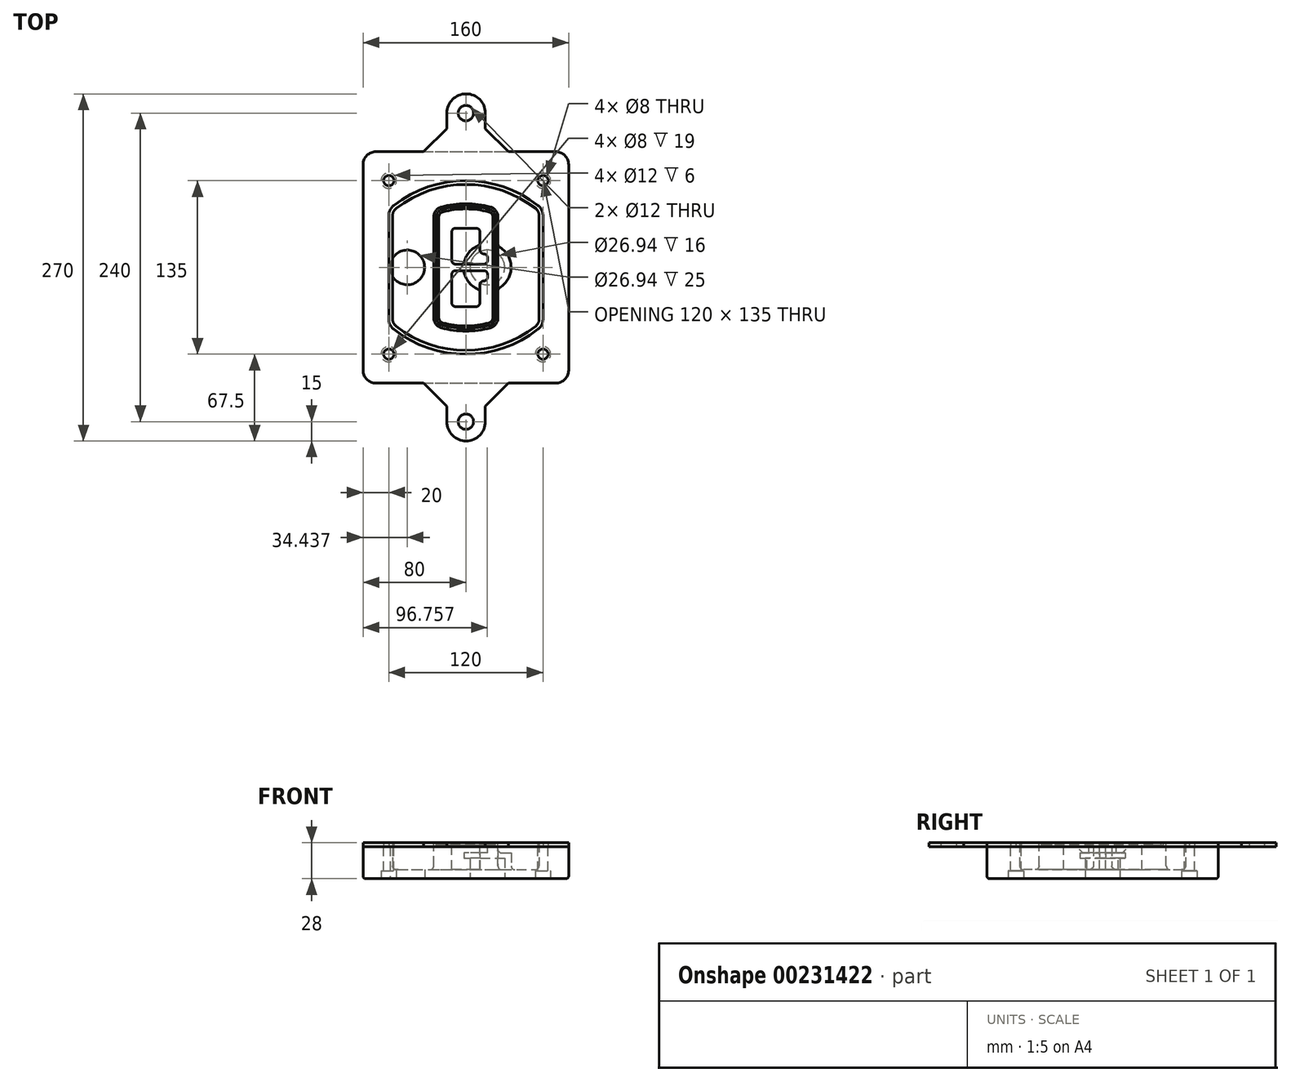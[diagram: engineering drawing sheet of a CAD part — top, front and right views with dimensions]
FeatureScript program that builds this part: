
annotation { "Feature Type Name" : "Feature", "Feature Type Description" : "" }
export const myFeature = defineFeature(function(context is Context, id is Id, definition is map)
    precondition{}
    {
        {
            var Q0;
            Q0=qCreatedBy(makeId("Top.planeOp"),FACE);
            var sketch = newSketch(context, id + "F0", { "sketchPlane" : qUnion([Q0])});
            skPoint(sketch, "E0.rect.middle", {"position": v(0, 0) * mm});
            skLineSegment(sketch, "E1.bottom", {"start": v(-70, -90) * mm, "end": v(70, -90) * mm});
            skLineSegment(sketch, "E1.top", {"start": v(-70, 90) * mm, "end": v(70, 90) * mm});
            skLineSegment(sketch, "E1.left", {"start": v(-80, -80) * mm, "end": v(-80, 80) * mm});
            skLineSegment(sketch, "E1.right", {"start": v(80, -80) * mm, "end": v(80, 80) * mm});
            skLineSegment(sketch, "E2", {"start": v(-80, 90) * mm, "end": v(80, -90) * mm, "construction": true});
            skLineSegment(sketch, "E3", {"start": v(80, 90) * mm, "end": v(-80, -90) * mm, "construction": true});
            skCircle(sketch, "E4", {"center": v(-60, 67.5) * mm, "radius": 4 * mm});
            skCircle(sketch, "E5", {"center": v(60, 67.5) * mm, "radius": 4 * mm});
            skCircle(sketch, "E6", {"center": v(60, -67.5) * mm, "radius": 4 * mm});
            skCircle(sketch, "E7", {"center": v(-60, -67.5) * mm, "radius": 4 * mm});
            skLineSegment(sketch, "E8", {"start": v(-60, 67.5) * mm, "end": v(60, 67.5) * mm, "construction": true});
            skLineSegment(sketch, "E9", {"start": v(60, 67.5) * mm, "end": v(60, -67.5) * mm, "construction": true});
            skLineSegment(sketch, "E10", {"start": v(60, -67.5) * mm, "end": v(-60, -67.5) * mm, "construction": true});
            skLineSegment(sketch, "E11", {"start": v(-60, -67.5) * mm, "end": v(-60, 67.5) * mm, "construction": true});
            skLineSegment(sketch, "E12", {"start": v(-60, 40.3) * mm, "end": v(-60, -40.3) * mm});
            skLineSegment(sketch, "E13", {"start": v(60, 40.3) * mm, "end": v(60, -40.3) * mm});
            skArc(sketch, "E14", {"start": v(56.15, 48.18) * mm, "mid": v(0, 67.5) * mm, "end": v(-56.15, 48.18) * mm});
            skArc(sketch, "E15", {"start": v(-56.15, -48.18) * mm, "mid": v(0, -67.5) * mm, "end": v(56.15, -48.18) * mm});
            skLineSegment(sketch, "E16", {"start": v(-60, 0) * mm, "end": v(60, 0) * mm, "construction": true});
            skPoint(sketch, "E17.visualSharp", {"position": v(-60, -45) * mm});
            skArc(sketch, "E17.filletArc", {"start": v(-60, -40.3) * mm, "mid": v(-58.99, -44.68) * mm, "end": v(-56.15, -48.18) * mm});
            skPoint(sketch, "E18.visualSharp", {"position": v(-60, 45) * mm});
            skArc(sketch, "E18.filletArc", {"start": v(-56.15, 48.18) * mm, "mid": v(-58.99, 44.68) * mm, "end": v(-60, 40.3) * mm});
            skPoint(sketch, "E19.visualSharp", {"position": v(60, 45) * mm});
            skArc(sketch, "E19.filletArc", {"start": v(60, 40.3) * mm, "mid": v(58.99, 44.68) * mm, "end": v(56.15, 48.18) * mm});
            skPoint(sketch, "E20.visualSharp", {"position": v(60, -45) * mm});
            skArc(sketch, "E20.filletArc", {"start": v(56.15, -48.18) * mm, "mid": v(58.99, -44.68) * mm, "end": v(60, -40.3) * mm});
            skPoint(sketch, "E21.visualSharp", {"position": v(-80, 90) * mm});
            skArc(sketch, "E21.filletArc", {"start": v(-70, 90) * mm, "mid": v(-77.07, 87.07) * mm, "end": v(-80, 80) * mm});
            skPoint(sketch, "E22.visualSharp", {"position": v(80, 90) * mm});
            skArc(sketch, "E22.filletArc", {"start": v(80, 80) * mm, "mid": v(77.07, 87.07) * mm, "end": v(70, 90) * mm});
            skPoint(sketch, "E23.visualSharp", {"position": v(80, -90) * mm});
            skArc(sketch, "E23.filletArc", {"start": v(70, -90) * mm, "mid": v(77.07, -87.07) * mm, "end": v(80, -80) * mm});
            skPoint(sketch, "E24.visualSharp", {"position": v(-80, -90) * mm});
            skArc(sketch, "E24.filletArc", {"start": v(-80, -80) * mm, "mid": v(-77.07, -87.07) * mm, "end": v(-70, -90) * mm});
            skArc(sketch, "E25.0", {"start": v(57, 40.3) * mm, "mid": v(56.3, 43.36) * mm, "end": v(54.3, 45.81) * mm});
            skLineSegment(sketch, "E25.1", {"start": v(57, 40.3) * mm, "end": v(57, -40.3) * mm});
            skArc(sketch, "E25.2", {"start": v(54.3, -45.81) * mm, "mid": v(56.3, -43.36) * mm, "end": v(57, -40.3) * mm});
            skArc(sketch, "E25.3", {"start": v(-54.3, -45.81) * mm, "mid": v(0, -64.5) * mm, "end": v(54.3, -45.81) * mm});
            skArc(sketch, "E25.4", {"start": v(-57, -40.3) * mm, "mid": v(-56.3, -43.36) * mm, "end": v(-54.3, -45.81) * mm});
            skArc(sketch, "E25.5", {"start": v(54.3, 45.81) * mm, "mid": v(0, 64.5) * mm, "end": v(-54.3, 45.81) * mm});
            skLineSegment(sketch, "E25.6", {"start": v(-57, 40.3) * mm, "end": v(-57, -40.3) * mm});
            skArc(sketch, "E25.7", {"start": v(-54.3, 45.81) * mm, "mid": v(-56.3, 43.36) * mm, "end": v(-57, 40.3) * mm});
            skArc(sketch, "E26.0", {"start": v(-58.62, 51.33) * mm, "mid": v(-62.58, 46.43) * mm, "end": v(-64, 40.3) * mm});
            skArc(sketch, "E26.1", {"start": v(58.62, 51.33) * mm, "mid": v(0, 71.5) * mm, "end": v(-58.62, 51.33) * mm});
            skArc(sketch, "E26.2", {"start": v(64, 40.3) * mm, "mid": v(62.58, 46.43) * mm, "end": v(58.62, 51.33) * mm});
            skLineSegment(sketch, "E26.3", {"start": v(64, 40.3) * mm, "end": v(64, -40.3) * mm});
            skArc(sketch, "E26.4", {"start": v(58.62, -51.33) * mm, "mid": v(62.58, -46.43) * mm, "end": v(64, -40.3) * mm});
            skLineSegment(sketch, "E26.5", {"start": v(-64, 40.3) * mm, "end": v(-64, -40.3) * mm});
            skArc(sketch, "E26.6", {"start": v(-58.62, -51.33) * mm, "mid": v(0, -71.5) * mm, "end": v(58.62, -51.33) * mm});
            skArc(sketch, "E26.7", {"start": v(-64, -40.3) * mm, "mid": v(-62.58, -46.43) * mm, "end": v(-58.62, -51.33) * mm});
            skSolve(sketch);
        }
        {
            var Q0;
            Q0=makeQuery(id+"F0.imprint","IMPRINT",FACE,{"disambiguationData":[TD([[makeQuery(id+"F0.imprint","IMPRINT",EDGE,{"derivedFrom":sQuery(id+"F0.wireOp",EDGE,"E1.bottom")}),1.0]])]});
            var Q1;
            Q1=makeQuery(id+"F0.imprint","IMPRINT",FACE,{"disambiguationData":[TD([[makeQuery(id+"F0.imprint","IMPRINT",EDGE,{"derivedFrom":sQuery(id+"F0.wireOp",EDGE,"E12")}),1.0]])]});
            var Q2;
            Q2=makeQuery(id+"F0.imprint","IMPRINT",FACE,{"disambiguationData":[TD([[makeQuery(id+"F0.imprint","IMPRINT",EDGE,{"derivedFrom":sQuery(id+"F0.wireOp",EDGE,"E25.0")}),1.0]])]});
            var Q3;
            Q3=makeQuery(id+"F0.imprint","IMPRINT",FACE,{"disambiguationData":[TD([[makeQuery(id+"F0.imprint","IMPRINT",EDGE,{"derivedFrom":sQuery(id+"F0.wireOp",EDGE,"E12")}),-1.0]])]});
            extrude(context, id + "F1", {"entities" : qUnion([Q0, Q1, Q2, Q3]), "oppositeDirection" : true, "depth" : 25 * mm});
        }
        {
            var Q0;
            Q0=makeQuery(id+"F0.imprint","IMPRINT",FACE,{"disambiguationData":[TD([[makeQuery(id+"F0.imprint","IMPRINT",EDGE,{"derivedFrom":sQuery(id+"F0.wireOp",EDGE,"E12")}),1.0]])]});
            extrude(context, id + "F2", {"entities" : qUnion([Q0]), "operationType" : NewBodyOperationType.ADD, "depth" : 3 * mm});
        }
        {
            var Q0;
            Q0=makeQuery(id+"F0.imprint","IMPRINT",FACE,{"disambiguationData":[TD([[makeQuery(id+"F0.imprint","IMPRINT",EDGE,{"derivedFrom":sQuery(id+"F0.wireOp",EDGE,"E25.0")}),1.0]])]});
            extrude(context, id + "F3", {"entities" : qUnion([Q0]), "operationType" : NewBodyOperationType.REMOVE, "oppositeDirection" : true, "depth" : 18 * mm});
        }
        {
            var Q0;
            Q0=makeQuery(id+"F2.opExtrude","CAP_FACE",FACE,{"disambiguationData":[OSD([sQuery(id+"F0.wireOp",EDGE,"E12"),sQuery(id+"F0.wireOp",EDGE,"E13"),sQuery(id+"F0.wireOp",EDGE,"E14"),sQuery(id+"F0.wireOp",EDGE,"E15"),sQuery(id+"F0.wireOp",EDGE,"E17.filletArc"),sQuery(id+"F0.wireOp",EDGE,"E18.filletArc"),sQuery(id+"F0.wireOp",EDGE,"E19.filletArc"),sQuery(id+"F0.wireOp",EDGE,"E20.filletArc"),sQuery(id+"F0.wireOp",EDGE,"E25.0"),sQuery(id+"F0.wireOp",EDGE,"E25.1"),sQuery(id+"F0.wireOp",EDGE,"E25.2"),sQuery(id+"F0.wireOp",EDGE,"E25.3"),sQuery(id+"F0.wireOp",EDGE,"E25.4"),sQuery(id+"F0.wireOp",EDGE,"E25.5"),sQuery(id+"F0.wireOp",EDGE,"E25.6"),sQuery(id+"F0.wireOp",EDGE,"E25.7")])],"isStart":false});
            var sketch = newSketch(context, id + "F4", { "sketchPlane" : qUnion([Q0])});
            skArc(sketch, "E27.0", {"start": v(-19.08, -46.97) * mm, "mid": v(0, -49.5) * mm, "end": v(19.08, -46.97) * mm});
            skArc(sketch, "E28.0", {"start": v(19.08, 46.97) * mm, "mid": v(0, 49.5) * mm, "end": v(-19.08, 46.97) * mm});
            skLineSegment(sketch, "E29", {"start": v(-25, 39.25) * mm, "end": v(-25, -39.25) * mm});
            skLineSegment(sketch, "E30", {"start": v(25, 39.25) * mm, "end": v(25, -39.25) * mm});
            skLineSegment(sketch, "E31", {"start": v(-25, 45.1) * mm, "end": v(25, 45.1) * mm, "construction": true});
            skLineSegment(sketch, "E32", {"start": v(-25, -45.1) * mm, "end": v(25, -45.1) * mm, "construction": true});
            skPoint(sketch, "E33.visualSharp", {"position": v(-25, 45.1) * mm});
            skArc(sketch, "E33.filletArc", {"start": v(-19.08, 46.97) * mm, "mid": v(-23.35, 44.11) * mm, "end": v(-25, 39.25) * mm});
            skPoint(sketch, "E34.visualSharp", {"position": v(25, 45.1) * mm});
            skArc(sketch, "E34.filletArc", {"start": v(25, 39.25) * mm, "mid": v(23.35, 44.11) * mm, "end": v(19.08, 46.97) * mm});
            skPoint(sketch, "E35.visualSharp", {"position": v(25, -45.1) * mm});
            skArc(sketch, "E35.filletArc", {"start": v(19.08, -46.97) * mm, "mid": v(23.35, -44.11) * mm, "end": v(25, -39.25) * mm});
            skPoint(sketch, "E36.visualSharp", {"position": v(-25, -45.1) * mm});
            skArc(sketch, "E36.filletArc", {"start": v(-25, -39.25) * mm, "mid": v(-23.35, -44.11) * mm, "end": v(-19.08, -46.97) * mm});
            skArc(sketch, "E37.0", {"start": v(54.3, 45.81) * mm, "mid": v(0, 64.5) * mm, "end": v(-54.3, 45.81) * mm});
            skArc(sketch, "E37.1", {"start": v(-54.3, 45.81) * mm, "mid": v(-56.3, 43.36) * mm, "end": v(-57, 40.3) * mm});
            skLineSegment(sketch, "E37.2", {"start": v(-57, 40.3) * mm, "end": v(-57, -40.3) * mm});
            skArc(sketch, "E37.3", {"start": v(-57, -40.3) * mm, "mid": v(-56.3, -43.36) * mm, "end": v(-54.3, -45.81) * mm});
            skArc(sketch, "E37.4", {"start": v(-54.3, -45.81) * mm, "mid": v(0, -64.5) * mm, "end": v(54.3, -45.81) * mm});
            skArc(sketch, "E37.5", {"start": v(54.3, -45.81) * mm, "mid": v(56.3, -43.36) * mm, "end": v(57, -40.3) * mm});
            skLineSegment(sketch, "E37.6", {"start": v(57, 40.3) * mm, "end": v(57, -40.3) * mm});
            skArc(sketch, "E37.7", {"start": v(57, 40.3) * mm, "mid": v(56.3, 43.36) * mm, "end": v(54.3, 45.81) * mm});
            skLineSegment(sketch, "E38.0", {"start": v(23, 39.25) * mm, "end": v(23, -39.25) * mm});
            skArc(sketch, "E38.1", {"start": v(18.56, -45.04) * mm, "mid": v(21.76, -42.9) * mm, "end": v(23, -39.25) * mm});
            skArc(sketch, "E38.2", {"start": v(-18.56, -45.04) * mm, "mid": v(0, -47.5) * mm, "end": v(18.56, -45.04) * mm});
            skArc(sketch, "E38.3", {"start": v(-23, -39.25) * mm, "mid": v(-21.76, -42.9) * mm, "end": v(-18.56, -45.04) * mm});
            skLineSegment(sketch, "E38.4", {"start": v(-23, 39.25) * mm, "end": v(-23, -39.25) * mm});
            skArc(sketch, "E38.5", {"start": v(23, 39.25) * mm, "mid": v(21.76, 42.9) * mm, "end": v(18.56, 45.04) * mm});
            skArc(sketch, "E38.6", {"start": v(-18.56, 45.04) * mm, "mid": v(-21.76, 42.9) * mm, "end": v(-23, 39.25) * mm});
            skArc(sketch, "E38.7", {"start": v(18.56, 45.04) * mm, "mid": v(0, 47.5) * mm, "end": v(-18.56, 45.04) * mm});
            skArc(sketch, "E39.0", {"start": v(21, 39.25) * mm, "mid": v(20.18, 41.68) * mm, "end": v(18.04, 43.1) * mm});
            skLineSegment(sketch, "E39.1", {"start": v(21, 39.25) * mm, "end": v(21, -39.25) * mm});
            skArc(sketch, "E39.2", {"start": v(18.04, -43.1) * mm, "mid": v(20.18, -41.68) * mm, "end": v(21, -39.25) * mm});
            skArc(sketch, "E39.3", {"start": v(-18.04, -43.1) * mm, "mid": v(0, -45.5) * mm, "end": v(18.04, -43.1) * mm});
            skArc(sketch, "E39.4", {"start": v(-21, -39.25) * mm, "mid": v(-20.18, -41.68) * mm, "end": v(-18.04, -43.1) * mm});
            skArc(sketch, "E39.5", {"start": v(18.04, 43.1) * mm, "mid": v(0, 45.5) * mm, "end": v(-18.04, 43.1) * mm});
            skLineSegment(sketch, "E39.6", {"start": v(-21, 39.25) * mm, "end": v(-21, -39.25) * mm});
            skArc(sketch, "E39.7", {"start": v(-18.04, 43.1) * mm, "mid": v(-20.18, 41.68) * mm, "end": v(-21, 39.25) * mm});
            skLineSegment(sketch, "E40", {"start": v(-25, 0) * mm, "end": v(25, 0) * mm, "construction": true});
            skLineSegment(sketch, "E41", {"start": v(-11, 5.5) * mm, "end": v(-11, 27.5) * mm});
            skLineSegment(sketch, "E42", {"start": v(-8, 30.5) * mm, "end": v(8, 30.5) * mm});
            skLineSegment(sketch, "E43", {"start": v(11, 27.5) * mm, "end": v(11, 13.5) * mm});
            skLineSegment(sketch, "E44", {"start": v(14, 10.5) * mm, "end": v(14, 10.5) * mm});
            skLineSegment(sketch, "E45", {"start": v(17, 7.5) * mm, "end": v(17, 5.5) * mm});
            skLineSegment(sketch, "E46", {"start": v(14, 2.5) * mm, "end": v(-8, 2.5) * mm});
            skPoint(sketch, "E47.visualSharp", {"position": v(-11, 30.5) * mm});
            skArc(sketch, "E47.filletArc", {"start": v(-8, 30.5) * mm, "mid": v(-10.12, 29.62) * mm, "end": v(-11, 27.5) * mm});
            skPoint(sketch, "E48.visualSharp", {"position": v(11, 30.5) * mm});
            skArc(sketch, "E48.filletArc", {"start": v(11, 27.5) * mm, "mid": v(10.12, 29.62) * mm, "end": v(8, 30.5) * mm});
            skPoint(sketch, "E49.visualSharp", {"position": v(11, 10.5) * mm});
            skArc(sketch, "E49.filletArc", {"start": v(11, 13.5) * mm, "mid": v(11.88, 11.38) * mm, "end": v(14, 10.5) * mm});
            skPoint(sketch, "E50.visualSharp", {"position": v(17, 10.5) * mm});
            skArc(sketch, "E50.filletArc", {"start": v(17, 7.5) * mm, "mid": v(16.12, 9.62) * mm, "end": v(14, 10.5) * mm});
            skPoint(sketch, "E51.visualSharp", {"position": v(17, 2.5) * mm});
            skArc(sketch, "E51.filletArc", {"start": v(14, 2.5) * mm, "mid": v(16.12, 3.38) * mm, "end": v(17, 5.5) * mm});
            skPoint(sketch, "E52.visualSharp", {"position": v(-11, 2.5) * mm});
            skArc(sketch, "E52.filletArc", {"start": v(-11, 5.5) * mm, "mid": v(-10.12, 3.38) * mm, "end": v(-8, 2.5) * mm});
            skLineSegment(sketch, "E53.0.MirrorCS", {"start": v(14, -2.5) * mm, "end": v(-8, -2.5) * mm});
            skArc(sketch, "E54.0.MirrorCS", {"start": v(-11, -5.5) * mm, "mid": v(-10.12, -3.38) * mm, "end": v(-8, -2.5) * mm});
            skLineSegment(sketch, "E55.0.MirrorCS", {"start": v(-11, -5.5) * mm, "end": v(-11, -27.5) * mm});
            skArc(sketch, "E56.0.MirrorCS", {"start": v(-8, -30.5) * mm, "mid": v(-10.12, -29.62) * mm, "end": v(-11, -27.5) * mm});
            skLineSegment(sketch, "E57.0.MirrorCS", {"start": v(-8, -30.5) * mm, "end": v(8, -30.5) * mm});
            skArc(sketch, "E58.0.MirrorCS", {"start": v(11, -27.5) * mm, "mid": v(10.12, -29.62) * mm, "end": v(8, -30.5) * mm});
            skLineSegment(sketch, "E59.0.MirrorCS", {"start": v(11, -27.5) * mm, "end": v(11, -13.5) * mm});
            skArc(sketch, "E60.0.MirrorCS", {"start": v(11, -13.5) * mm, "mid": v(11.88, -11.38) * mm, "end": v(14, -10.5) * mm});
            skArc(sketch, "E61.0.MirrorCS", {"start": v(17, -7.5) * mm, "mid": v(16.12, -9.62) * mm, "end": v(14, -10.5) * mm});
            skLineSegment(sketch, "E62.0.MirrorCS", {"start": v(17, -7.5) * mm, "end": v(17, -5.5) * mm});
            skArc(sketch, "E63.0.MirrorCS", {"start": v(14, -2.5) * mm, "mid": v(16.12, -3.38) * mm, "end": v(17, -5.5) * mm});
            skSolve(sketch);
        }
        {
            var Q0;
            Q0=makeQuery(id+"F4.imprint","IMPRINT",FACE,{"disambiguationData":[TD([[makeQuery(id+"F4.imprint","IMPRINT",EDGE,{"derivedFrom":sQuery(id+"F4.wireOp",EDGE,"E27.0")}),1.0]])]});
            var Q1;
            Q1=makeQuery(id+"F4.imprint","IMPRINT",FACE,{"disambiguationData":[TD([[makeQuery(id+"F4.imprint","IMPRINT",EDGE,{"derivedFrom":sQuery(id+"F4.wireOp",EDGE,"E38.0")}),-1.0]])]});
            var Q2;
            Q2=makeQuery(id+"F4.imprint","IMPRINT",FACE,{"disambiguationData":[TD([[makeQuery(id+"F4.imprint","IMPRINT",EDGE,{"derivedFrom":sQuery(id+"F4.wireOp",EDGE,"E39.0")}),1.0]])]});
            extrude(context, id + "F5", {"entities" : qUnion([Q0, Q1, Q2]), "operationType" : NewBodyOperationType.ADD, "endBound" : BoundingType.UP_TO_NEXT, "oppositeDirection" : true, "depth" : 25 * mm});
        }
        {
            var Q0;
            Q0=makeQuery(id+"F4.imprint","IMPRINT",FACE,{"disambiguationData":[TD([[makeQuery(id+"F4.imprint","IMPRINT",EDGE,{"derivedFrom":sQuery(id+"F4.wireOp",EDGE,"E38.0")}),-1.0]])]});
            extrude(context, id + "F6", {"entities" : qUnion([Q0]), "operationType" : NewBodyOperationType.REMOVE, "oppositeDirection" : true, "depth" : 2 * mm});
        }
        {
            var Q0;
            Q0=makeQuery(id+"F1.opExtrude","CAP_FACE",FACE,{"disambiguationData":[OSD([sQuery(id+"F0.wireOp",EDGE,"E1.bottom"),sQuery(id+"F0.wireOp",EDGE,"E1.top"),sQuery(id+"F0.wireOp",EDGE,"E1.left"),sQuery(id+"F0.wireOp",EDGE,"E1.right"),sQuery(id+"F0.wireOp",EDGE,"E4"),sQuery(id+"F0.wireOp",EDGE,"E5"),sQuery(id+"F0.wireOp",EDGE,"E6"),sQuery(id+"F0.wireOp",EDGE,"E7"),sQuery(id+"F0.wireOp",EDGE,"E21.filletArc"),sQuery(id+"F0.wireOp",EDGE,"E22.filletArc"),sQuery(id+"F0.wireOp",EDGE,"E23.filletArc"),sQuery(id+"F0.wireOp",EDGE,"E24.filletArc")])],"isStart":false});
            var sketch = newSketch(context, id + "F7", { "sketchPlane" : qUnion([Q0])});
            skCircle(sketch, "E64", {"center": v(16.76, 0) * mm, "radius": 13.47 * mm});
            skCircle(sketch, "E65", {"center": v(-45.56, 0) * mm, "radius": 13.47 * mm});
            skLineSegment(sketch, "E66", {"start": v(80, 0) * mm, "end": v(-80, 0) * mm});
            skCircle(sketch, "E67", {"center": v(16.76, 0) * mm, "radius": 18.47 * mm});
            skCircle(sketch, "E68", {"center": v(60, -67.5) * mm, "radius": 6 * mm});
            skCircle(sketch, "E69", {"center": v(-60, -67.5) * mm, "radius": 6 * mm});
            skCircle(sketch, "E70", {"center": v(-60, 67.5) * mm, "radius": 6 * mm});
            skCircle(sketch, "E71", {"center": v(60, 67.5) * mm, "radius": 6 * mm});
            skSolve(sketch);
        }
        {
            var Q0;
            {var subQ1=sQuery(id+"F7.wireOp",EDGE,"E66");var subQ4=sQuery(id+"F7.wireOp",EDGE,"E64");var subQ6=makeQuery(id+"F7.imprint","INTERSECT",VERTEX,{"disambiguationData":[OD(0.0)],"derivedFrom":[subQ4,subQ1]});Q0=makeQuery(id+"F7.imprint","IMPRINT",FACE,{"disambiguationData":[TD([[makeQuery(id+"F7.imprint","IMPRINT",EDGE,{"disambiguationData":[TD([[subQ6,-1.0]])],"derivedFrom":subQ4}),-1.0]])]});}
            var Q1;
            {var subQ0=sQuery(id+"F7.wireOp",EDGE,"E66");var subQ1=sQuery(id+"F7.wireOp",EDGE,"E64");var subQ3=makeQuery(id+"F7.imprint","INTERSECT",VERTEX,{"disambiguationData":[OD(0.0)],"derivedFrom":[subQ1,subQ0]});Q1=makeQuery(id+"F7.imprint","IMPRINT",FACE,{"disambiguationData":[TD([[makeQuery(id+"F7.imprint","IMPRINT",EDGE,{"disambiguationData":[TD([[subQ3,-1.0]])],"derivedFrom":subQ1}),1.0]])]});}
            var Q2;
            {var subQ0=sQuery(id+"F7.wireOp",EDGE,"E66");var subQ1=sQuery(id+"F7.wireOp",EDGE,"E64");var subQ3=makeQuery(id+"F7.imprint","INTERSECT",VERTEX,{"disambiguationData":[OD(0.0)],"derivedFrom":[subQ1,subQ0]});Q2=makeQuery(id+"F7.imprint","IMPRINT",FACE,{"disambiguationData":[TD([[makeQuery(id+"F7.imprint","IMPRINT",EDGE,{"disambiguationData":[TD([[subQ3,1.0]])],"derivedFrom":subQ1}),1.0]])]});}
            var Q3;
            {var subQ1=sQuery(id+"F7.wireOp",EDGE,"E66");var subQ4=sQuery(id+"F7.wireOp",EDGE,"E64");var subQ6=makeQuery(id+"F7.imprint","INTERSECT",VERTEX,{"disambiguationData":[OD(0.0)],"derivedFrom":[subQ4,subQ1]});Q3=makeQuery(id+"F7.imprint","IMPRINT",FACE,{"disambiguationData":[TD([[makeQuery(id+"F7.imprint","IMPRINT",EDGE,{"disambiguationData":[TD([[subQ6,1.0]])],"derivedFrom":subQ4}),-1.0]])]});}
            extrude(context, id + "F8", {"entities" : qUnion([Q0, Q1, Q2, Q3]), "operationType" : NewBodyOperationType.ADD, "oppositeDirection" : true, "depth" : 20 * mm});
        }
        {
            var Q0;
            {var subQ0=sQuery(id+"F7.wireOp",EDGE,"E66");var subQ1=sQuery(id+"F7.wireOp",EDGE,"E64");var subQ3=makeQuery(id+"F7.imprint","INTERSECT",VERTEX,{"disambiguationData":[OD(0.0)],"derivedFrom":[subQ1,subQ0]});Q0=makeQuery(id+"F7.imprint","IMPRINT",FACE,{"disambiguationData":[TD([[makeQuery(id+"F7.imprint","IMPRINT",EDGE,{"disambiguationData":[TD([[subQ3,-1.0]])],"derivedFrom":subQ1}),1.0]])]});}
            var Q1;
            {var subQ0=sQuery(id+"F7.wireOp",EDGE,"E66");var subQ1=sQuery(id+"F7.wireOp",EDGE,"E64");var subQ3=makeQuery(id+"F7.imprint","INTERSECT",VERTEX,{"disambiguationData":[OD(0.0)],"derivedFrom":[subQ1,subQ0]});Q1=makeQuery(id+"F7.imprint","IMPRINT",FACE,{"disambiguationData":[TD([[makeQuery(id+"F7.imprint","IMPRINT",EDGE,{"disambiguationData":[TD([[subQ3,1.0]])],"derivedFrom":subQ1}),1.0]])]});}
            extrude(context, id + "F9", {"entities" : qUnion([Q0, Q1]), "operationType" : NewBodyOperationType.REMOVE, "oppositeDirection" : true, "depth" : 16 * mm});
        }
        {
            var Q0;
            {var subQ0=sQuery(id+"F7.wireOp",EDGE,"E66");var subQ1=sQuery(id+"F7.wireOp",EDGE,"E65");var subQ3=makeQuery(id+"F7.imprint","INTERSECT",VERTEX,{"disambiguationData":[OD(0.0)],"derivedFrom":[subQ1,subQ0]});Q0=makeQuery(id+"F7.imprint","IMPRINT",FACE,{"disambiguationData":[TD([[makeQuery(id+"F7.imprint","IMPRINT",EDGE,{"disambiguationData":[TD([[subQ3,-1.0]])],"derivedFrom":subQ1}),1.0]])]});}
            var Q1;
            {var subQ0=sQuery(id+"F7.wireOp",EDGE,"E66");var subQ1=sQuery(id+"F7.wireOp",EDGE,"E65");var subQ3=makeQuery(id+"F7.imprint","INTERSECT",VERTEX,{"disambiguationData":[OD(0.0)],"derivedFrom":[subQ1,subQ0]});Q1=makeQuery(id+"F7.imprint","IMPRINT",FACE,{"disambiguationData":[TD([[makeQuery(id+"F7.imprint","IMPRINT",EDGE,{"disambiguationData":[TD([[subQ3,1.0]])],"derivedFrom":subQ1}),1.0]])]});}
            extrude(context, id + "F10", {"entities" : qUnion([Q0, Q1]), "operationType" : NewBodyOperationType.REMOVE, "oppositeDirection" : true, "depth" : 25 * mm});
        }
        {
            var Q0;
            Q0=makeQuery(id+"F7.imprint","IMPRINT",FACE,{"disambiguationData":[TD([[makeQuery(id+"F7.imprint","IMPRINT",EDGE,{"derivedFrom":sQuery(id+"F7.wireOp",EDGE,"E68")}),1.0]])]});
            var Q1;
            Q1=makeQuery(id+"F7.imprint","IMPRINT",FACE,{"disambiguationData":[TD([[makeQuery(id+"F7.imprint","IMPRINT",EDGE,{"derivedFrom":makeQuery(id+"F1.opExtrude","CAP_EDGE",EDGE,{"disambiguationData":[OSD([sQuery(id+"F0.wireOp",EDGE,"E5")])],"isStart":false})}),-1.0]])]});
            var Q2;
            Q2=makeQuery(id+"F7.imprint","IMPRINT",FACE,{"disambiguationData":[TD([[makeQuery(id+"F7.imprint","IMPRINT",EDGE,{"derivedFrom":sQuery(id+"F7.wireOp",EDGE,"E69")}),1.0]])]});
            var Q3;
            Q3=makeQuery(id+"F7.imprint","IMPRINT",FACE,{"disambiguationData":[TD([[makeQuery(id+"F7.imprint","IMPRINT",EDGE,{"derivedFrom":makeQuery(id+"F1.opExtrude","CAP_EDGE",EDGE,{"disambiguationData":[OSD([sQuery(id+"F0.wireOp",EDGE,"E4")])],"isStart":false})}),-1.0]])]});
            var Q4;
            Q4=makeQuery(id+"F7.imprint","IMPRINT",FACE,{"disambiguationData":[TD([[makeQuery(id+"F7.imprint","IMPRINT",EDGE,{"derivedFrom":sQuery(id+"F7.wireOp",EDGE,"E70")}),1.0]])]});
            var Q5;
            Q5=makeQuery(id+"F7.imprint","IMPRINT",FACE,{"disambiguationData":[TD([[makeQuery(id+"F7.imprint","IMPRINT",EDGE,{"derivedFrom":makeQuery(id+"F1.opExtrude","CAP_EDGE",EDGE,{"disambiguationData":[OSD([sQuery(id+"F0.wireOp",EDGE,"E7")])],"isStart":false})}),-1.0]])]});
            var Q6;
            Q6=makeQuery(id+"F7.imprint","IMPRINT",FACE,{"disambiguationData":[TD([[makeQuery(id+"F7.imprint","IMPRINT",EDGE,{"derivedFrom":sQuery(id+"F7.wireOp",EDGE,"E71")}),1.0]])]});
            var Q7;
            Q7=makeQuery(id+"F7.imprint","IMPRINT",FACE,{"disambiguationData":[TD([[makeQuery(id+"F7.imprint","IMPRINT",EDGE,{"derivedFrom":makeQuery(id+"F1.opExtrude","CAP_EDGE",EDGE,{"disambiguationData":[OSD([sQuery(id+"F0.wireOp",EDGE,"E6")])],"isStart":false})}),-1.0]])]});
            extrude(context, id + "F11", {"entities" : qUnion([Q0, Q1, Q2, Q3, Q4, Q5, Q6, Q7]), "operationType" : NewBodyOperationType.REMOVE, "oppositeDirection" : true, "depth" : 6 * mm});
        }
        {
            var Q0;
            Q0=makeQuery(id+"F9.boolean.opBoolean","COPY",FACE,{"derivedFrom":makeQuery(id+"F9.opExtrude","CAP_FACE",FACE,{"disambiguationData":[OSD([sQuery(id+"F7.wireOp",EDGE,"E64")])],"isStart":false})});
            var sketch = newSketch(context, id + "F12", { "sketchPlane" : qUnion([Q0])});
            skArc(sketch, "E72.0", {"start": v(11, 17.55) * mm, "mid": v(2.57, 11.82) * mm, "end": v(-1.54, 2.5) * mm});
            skArc(sketch, "E72.1", {"start": v(-1.54, -2.5) * mm, "mid": v(2.57, -11.82) * mm, "end": v(11, -17.55) * mm});
            skLineSegment(sketch, "E73", {"start": v(-1.54, -2.5) * mm, "end": v(14, -2.5) * mm});
            skLineSegment(sketch, "E74.0", {"start": v(14, 2.5) * mm, "end": v(-1.54, 2.5) * mm});
            skArc(sketch, "E74.1", {"start": v(14, 2.5) * mm, "mid": v(16.12, 3.38) * mm, "end": v(17, 5.5) * mm});
            skLineSegment(sketch, "E74.2", {"start": v(17, 7.5) * mm, "end": v(17, 5.5) * mm});
            skArc(sketch, "E74.3", {"start": v(17, 7.5) * mm, "mid": v(16.12, 9.62) * mm, "end": v(14, 10.5) * mm});
            skArc(sketch, "E74.4", {"start": v(11, 13.5) * mm, "mid": v(11.88, 11.38) * mm, "end": v(14, 10.5) * mm});
            skLineSegment(sketch, "E74.5", {"start": v(11, 17.55) * mm, "end": v(11, 13.5) * mm});
            skLineSegment(sketch, "E74.7", {"start": v(14, -2.5) * mm, "end": v(-1.54, -2.5) * mm});
            skArc(sketch, "E74.8", {"start": v(14, -2.5) * mm, "mid": v(16.12, -3.38) * mm, "end": v(17, -5.5) * mm});
            skLineSegment(sketch, "E74.9", {"start": v(17, -7.5) * mm, "end": v(17, -5.5) * mm});
            skArc(sketch, "E74.10", {"start": v(17, -7.5) * mm, "mid": v(16.12, -9.62) * mm, "end": v(14, -10.5) * mm});
            skArc(sketch, "E74.11", {"start": v(11, -13.5) * mm, "mid": v(11.88, -11.38) * mm, "end": v(14, -10.5) * mm});
            skLineSegment(sketch, "E74.12", {"start": v(11, -17.55) * mm, "end": v(11, -13.5) * mm});
            skPoint(sketch, "E75.orphan", {"position": v(11, -27.5) * mm});
            skPoint(sketch, "E76.orphan", {"position": v(-8, -2.5) * mm});
            skPoint(sketch, "E77.orphan", {"position": v(-8, 2.5) * mm});
            skPoint(sketch, "E78.orphan", {"position": v(11, 27.5) * mm});
            skSolve(sketch);
        }
        {
            var Q0;
            {var subQ7=sQuery(id+"F12.wireOp",EDGE,"E72.0");var subQ14=sQuery(id+"F12.wireOp",EDGE,"E72.1");var subQ16=sQuery(id+"F12.wireOp",EDGE,"E74.1");var subQ18=sQuery(id+"F12.wireOp",EDGE,"E74.8");Q0=qUnion([makeQuery(id+"F12.imprint","IMPRINT",FACE,{"disambiguationData":[TD([[makeQuery(id+"F12.imprint","IMPRINT",EDGE,{"derivedFrom":subQ7}),1.0]])]}),makeQuery(id+"F12.imprint","IMPRINT",FACE,{"disambiguationData":[TD([[makeQuery(id+"F12.imprint","IMPRINT",EDGE,{"derivedFrom":subQ14}),1.0]])]}),makeQuery(id+"F12.imprint","IMPRINT",FACE,{"disambiguationData":[TD([[makeQuery(id+"F12.imprint","IMPRINT",EDGE,{"derivedFrom":subQ16}),1.0]])]}),makeQuery(id+"F12.imprint","IMPRINT",FACE,{"disambiguationData":[TD([[makeQuery(id+"F12.imprint","IMPRINT",EDGE,{"derivedFrom":subQ18}),-1.0]])]})]);}
            var Q1;
            Q1=makeQuery(id+"F5.boolean.opBoolean","SPLIT",FACE,{"disambiguationData":[TD([makeQuery(id+"F5.opExtrude","SWEPT_FACE",FACE,{"disambiguationData":[OSD([sQuery(id+"F4.wireOp",EDGE,"E41")])]})])],"derivedFrom":makeQuery(id+"F3.boolean.opBoolean","COPY",FACE,{"derivedFrom":makeQuery(id+"F3.opExtrude","CAP_FACE",FACE,{"disambiguationData":[OSD([sQuery(id+"F0.wireOp",EDGE,"E25.0"),sQuery(id+"F0.wireOp",EDGE,"E25.1"),sQuery(id+"F0.wireOp",EDGE,"E25.2"),sQuery(id+"F0.wireOp",EDGE,"E25.3"),sQuery(id+"F0.wireOp",EDGE,"E25.4"),sQuery(id+"F0.wireOp",EDGE,"E25.5"),sQuery(id+"F0.wireOp",EDGE,"E25.6"),sQuery(id+"F0.wireOp",EDGE,"E25.7")])],"isStart":false})})});
            extrude(context, id + "F13", {"entities" : qUnion([Q0]), "operationType" : NewBodyOperationType.REMOVE, "endBound" : BoundingType.UP_TO_SURFACE, "endBoundEntityFace" : qUnion([Q1]), "depth" : 25 * mm});
        }
        {
            var Q0;
            Q0=makeQuery(id+"F3.boolean.opBoolean","COPY",EDGE,{"derivedFrom":makeQuery(id+"F3.opExtrude","CAP_EDGE",EDGE,{"disambiguationData":[OSD([sQuery(id+"F0.wireOp",EDGE,"E25.6")])],"isStart":false})});
            var Q1;
            Q1=makeQuery(id+"F8.boolean.opBoolean","INTERSECT",EDGE,{"derivedFrom":[makeQuery(id+"F5.opExtrude","SWEPT_FACE",FACE,{"disambiguationData":[OSD([sQuery(id+"F4.wireOp",EDGE,"E30")])]}),makeQuery(id+"F8.opExtrude","CAP_FACE",FACE,{"disambiguationData":[OSD([sQuery(id+"F7.wireOp",EDGE,"E67")])],"isStart":false})]});
            var Q2;
            Q2=makeQuery(id+"F8.boolean.opBoolean","INTERSECT",EDGE,{"disambiguationData":[OD(1.0)],"derivedFrom":[makeQuery(id+"F5.opExtrude","SWEPT_FACE",FACE,{"disambiguationData":[OSD([sQuery(id+"F4.wireOp",EDGE,"E30")])]}),makeQuery(id+"F8.opExtrude","SWEPT_FACE",FACE,{"disambiguationData":[OSD([sQuery(id+"F7.wireOp",EDGE,"E67")])]})]});
            var Q3;
            {var subQ0=sQuery(id+"F4.wireOp",EDGE,"E30");Q3=makeQuery(id+"F8.boolean.opBoolean","SPLIT",EDGE,{"disambiguationData":[TD([makeQuery(id+"F5.opExtrude","SWEPT_FACE",FACE,{"disambiguationData":[OSD([sQuery(id+"F4.wireOp",EDGE,"E35.filletArc")])]})])],"derivedFrom":makeQuery(id+"F5.opExtrude","CAP_EDGE",EDGE,{"disambiguationData":[OSD([subQ0])],"isStart":false})});}
            var Q4;
            {var subQ0=sQuery(id+"F0.wireOp",EDGE,"E25.7");var subQ1=sQuery(id+"F0.wireOp",EDGE,"E25.1");var subQ2=sQuery(id+"F0.wireOp",EDGE,"E25.6");var subQ3=sQuery(id+"F0.wireOp",EDGE,"E25.5");var subQ4=sQuery(id+"F0.wireOp",EDGE,"E25.4");var subQ5=sQuery(id+"F0.wireOp",EDGE,"E25.0");var subQ6=sQuery(id+"F0.wireOp",EDGE,"E25.2");var subQ7=sQuery(id+"F0.wireOp",EDGE,"E25.3");Q4=makeQuery(id+"F8.boolean.opBoolean","INTERSECT",EDGE,{"derivedFrom":[makeQuery(id+"F5.boolean.opBoolean","SPLIT",FACE,{"disambiguationData":[TD([makeQuery(id+"F2.opExtrude","SWEPT_FACE",FACE,{"disambiguationData":[OSD([subQ5])]})])],"derivedFrom":makeQuery(id+"F3.boolean.opBoolean","COPY",FACE,{"derivedFrom":makeQuery(id+"F3.opExtrude","CAP_FACE",FACE,{"disambiguationData":[OSD([subQ5,subQ1,subQ6,subQ7,subQ4,subQ3,subQ2,subQ0])],"isStart":false})})}),makeQuery(id+"F8.opExtrude","SWEPT_FACE",FACE,{"disambiguationData":[OSD([sQuery(id+"F7.wireOp",EDGE,"E67")])]})]});}
            var Q5;
            Q5=makeQuery(id+"F8.boolean.opBoolean","INTERSECT",EDGE,{"disambiguationData":[OD(0.0)],"derivedFrom":[makeQuery(id+"F5.opExtrude","SWEPT_FACE",FACE,{"disambiguationData":[OSD([sQuery(id+"F4.wireOp",EDGE,"E30")])]}),makeQuery(id+"F8.opExtrude","SWEPT_FACE",FACE,{"disambiguationData":[OSD([sQuery(id+"F7.wireOp",EDGE,"E67")])]})]});
            fillet(context, id + "F14", {"entities" : qUnion([Q0, Q1, Q2, Q3, Q4, Q5]), "radius" : 3 * mm, "tangentPropagation" : true, "allowEdgeOverflow" : false});
        }
        {
            var Q0;
            Q0=makeQuery(id+"F1.opExtrude","CAP_EDGE",EDGE,{"disambiguationData":[OSD([sQuery(id+"F0.wireOp",EDGE,"E1.bottom")])],"isStart":false});
            fillet(context, id + "F15", {"entities" : qUnion([Q0]), "radius" : 2 * mm, "tangentPropagation" : true, "allowEdgeOverflow" : false});
        }
        {
            var Q0;
            {var subQ0=sQuery(id+"F0.wireOp",EDGE,"E22.filletArc");var subQ1=sQuery(id+"F0.wireOp",EDGE,"E7");var subQ2=sQuery(id+"F0.wireOp",EDGE,"E6");var subQ3=sQuery(id+"F0.wireOp",EDGE,"E5");var subQ4=sQuery(id+"F0.wireOp",EDGE,"E4");var subQ5=sQuery(id+"F0.wireOp",EDGE,"E1.bottom");var subQ6=sQuery(id+"F0.wireOp",EDGE,"E21.filletArc");var subQ7=sQuery(id+"F0.wireOp",EDGE,"E1.top");var subQ8=sQuery(id+"F0.wireOp",EDGE,"E1.left");var subQ9=sQuery(id+"F0.wireOp",EDGE,"E1.right");var subQ10=sQuery(id+"F0.wireOp",EDGE,"E23.filletArc");var subQ11=sQuery(id+"F0.wireOp",EDGE,"E24.filletArc");Q0=makeQuery(id+"F2.boolean.opBoolean","SPLIT",FACE,{"disambiguationData":[TD([makeQuery(id+"F1.opExtrude","SWEPT_FACE",FACE,{"disambiguationData":[OSD([subQ5])]})])],"derivedFrom":makeQuery(id+"F1.opExtrude","CAP_FACE",FACE,{"disambiguationData":[OSD([subQ5,subQ7,subQ8,subQ9,subQ4,subQ3,subQ2,subQ1,subQ6,subQ0,subQ10,subQ11])],"isStart":true})});}
            var sketch = newSketch(context, id + "F16", { "sketchPlane" : qUnion([Q0])});
            skLineSegment(sketch, "E79", {"start": v(0, 90) * mm, "end": v(0, 120) * mm});
            skCircle(sketch, "E80", {"center": v(0, 120) * mm, "radius": 6 * mm});
            skLineSegment(sketch, "E81", {"start": v(-14.82, 120) * mm, "end": v(-14.82, 108) * mm});
            skLineSegment(sketch, "E82", {"start": v(-14.82, 108) * mm, "end": v(-32.82, 90) * mm});
            skLineSegment(sketch, "E83", {"start": v(15.18, 120) * mm, "end": v(15.18, 108) * mm});
            skLineSegment(sketch, "E84", {"start": v(15.18, 108) * mm, "end": v(33.18, 90) * mm});
            skArc(sketch, "E85", {"start": v(15.18, 120) * mm, "mid": v(0.18, 135) * mm, "end": v(-14.82, 120) * mm});
            skLineSegment(sketch, "E86", {"start": v(-32.82, 90) * mm, "end": v(33.18, 90) * mm});
            skLineSegment(sketch, "E87", {"start": v(-95.32, 0) * mm, "end": v(97, 0) * mm, "construction": true});
            skPoint(sketch, "E87.startSnap0", {"position": v(-80, 0) * mm});
            skPoint(sketch, "E87.endSnap0", {"position": v(-80, 0) * mm});
            skLineSegment(sketch, "E88.MirrorCS", {"start": v(-14.82, -108) * mm, "end": v(-32.82, -90) * mm});
            skLineSegment(sketch, "E89.MirrorCS", {"start": v(-14.82, -120) * mm, "end": v(-14.82, -108) * mm});
            skLineSegment(sketch, "E90.MirrorCS", {"start": v(15.18, -120) * mm, "end": v(15.18, -108) * mm});
            skArc(sketch, "E91.MirrorCS", {"start": v(15.18, -120) * mm, "mid": v(0.18, -135) * mm, "end": v(-14.82, -120) * mm});
            skLineSegment(sketch, "E92.MirrorCS", {"start": v(-32.82, -90) * mm, "end": v(33.18, -90) * mm});
            skLineSegment(sketch, "E93.MirrorCS", {"start": v(15.18, -108) * mm, "end": v(33.18, -90) * mm});
            skLineSegment(sketch, "E94.MirrorCS", {"start": v(0, -90) * mm, "end": v(0, -120) * mm});
            skCircle(sketch, "E95.MirrorC", {"center": v(0, -120) * mm, "radius": 6 * mm});
            skSolve(sketch);
        }
        {
            var Q0;
            Q0=makeQuery(id+"F16.imprint","IMPRINT",FACE,{"disambiguationData":[TD([[makeQuery(id+"F16.imprint","IMPRINT",EDGE,{"derivedFrom":sQuery(id+"F16.wireOp",EDGE,"E80")}),-1.0]])]});
            var Q1;
            {var subQ0=sQuery(id+"F16.wireOp",EDGE,"E88.MirrorCS");Q1=makeQuery(id+"F16.imprint","IMPRINT",FACE,{"disambiguationData":[TD([[makeQuery(id+"F16.imprint","IMPRINT",EDGE,{"derivedFrom":subQ0}),-1.0]])]});}
            var Q2;
            Q2=makeQuery(id+"F16.imprint","IMPRINT",FACE,{"disambiguationData":[TD([[makeQuery(id+"F16.imprint","IMPRINT",EDGE,{"derivedFrom":makeQuery(id+"F1.opExtrude","CAP_EDGE",EDGE,{"disambiguationData":[OSD([sQuery(id+"F0.wireOp",EDGE,"E1.left")])],"isStart":true})}),-1.0]])]});
            var Q3;
            Q3=makeQuery(id+"F2.opExtrude","CAP_FACE",FACE,{"disambiguationData":[OSD([sQuery(id+"F0.wireOp",EDGE,"E12"),sQuery(id+"F0.wireOp",EDGE,"E13"),sQuery(id+"F0.wireOp",EDGE,"E14"),sQuery(id+"F0.wireOp",EDGE,"E15"),sQuery(id+"F0.wireOp",EDGE,"E17.filletArc"),sQuery(id+"F0.wireOp",EDGE,"E18.filletArc"),sQuery(id+"F0.wireOp",EDGE,"E19.filletArc"),sQuery(id+"F0.wireOp",EDGE,"E20.filletArc"),sQuery(id+"F0.wireOp",EDGE,"E25.0"),sQuery(id+"F0.wireOp",EDGE,"E25.1"),sQuery(id+"F0.wireOp",EDGE,"E25.2"),sQuery(id+"F0.wireOp",EDGE,"E25.3"),sQuery(id+"F0.wireOp",EDGE,"E25.4"),sQuery(id+"F0.wireOp",EDGE,"E25.5"),sQuery(id+"F0.wireOp",EDGE,"E25.6"),sQuery(id+"F0.wireOp",EDGE,"E25.7")])],"isStart":false});
            extrude(context, id + "F17", {"entities" : qUnion([Q0, Q1, Q2]), "endBound" : BoundingType.UP_TO_SURFACE, "endBoundEntityFace" : qUnion([Q3]), "depth" : 25 * mm});
        }
    });
